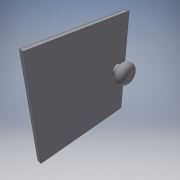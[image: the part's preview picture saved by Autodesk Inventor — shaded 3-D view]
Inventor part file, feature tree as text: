
AUTODESK INVENTOR PART (.ipt)
format: ipt  version: 2016 (Build 200138000, 138)  size: 114,176 bytes
history: native  units: in
note: dims shown in document units (in); Inventor stores cm internally (conversion verified against a paired STEP export)
features: extrude x3, sketch x3, fillet x1
ambient origin geometry x8: Origin, YZ Plane, XZ Plane, XY Plane, X Axis, Y Axis, Z Axis, Center Point
bodies: Solid1 (feature_tree)
feature tree (7):
  extrude  "Extrusion1"  Depth=18.0in
  extrude  "Extrusion2"  Depth=0.75in
  extrude  "Extrusion3"  Depth=0.75in TaperAngle=0.0deg
  fillet  "Fillet1"  Radius=2.0in
  sketch  "Sketch1"  dims[d0=18.0in d1=18.0in]
  sketch  "Sketch2"  dims[d2=0.75in d3=0.0in d4=2.0in]
  sketch  "Sketch3"  dims[d5=2.0in d6=0.75in d7=0.0in d8=2.0in d9=4.0in d10=2.0in d11=0.0in d12=1.0in]
